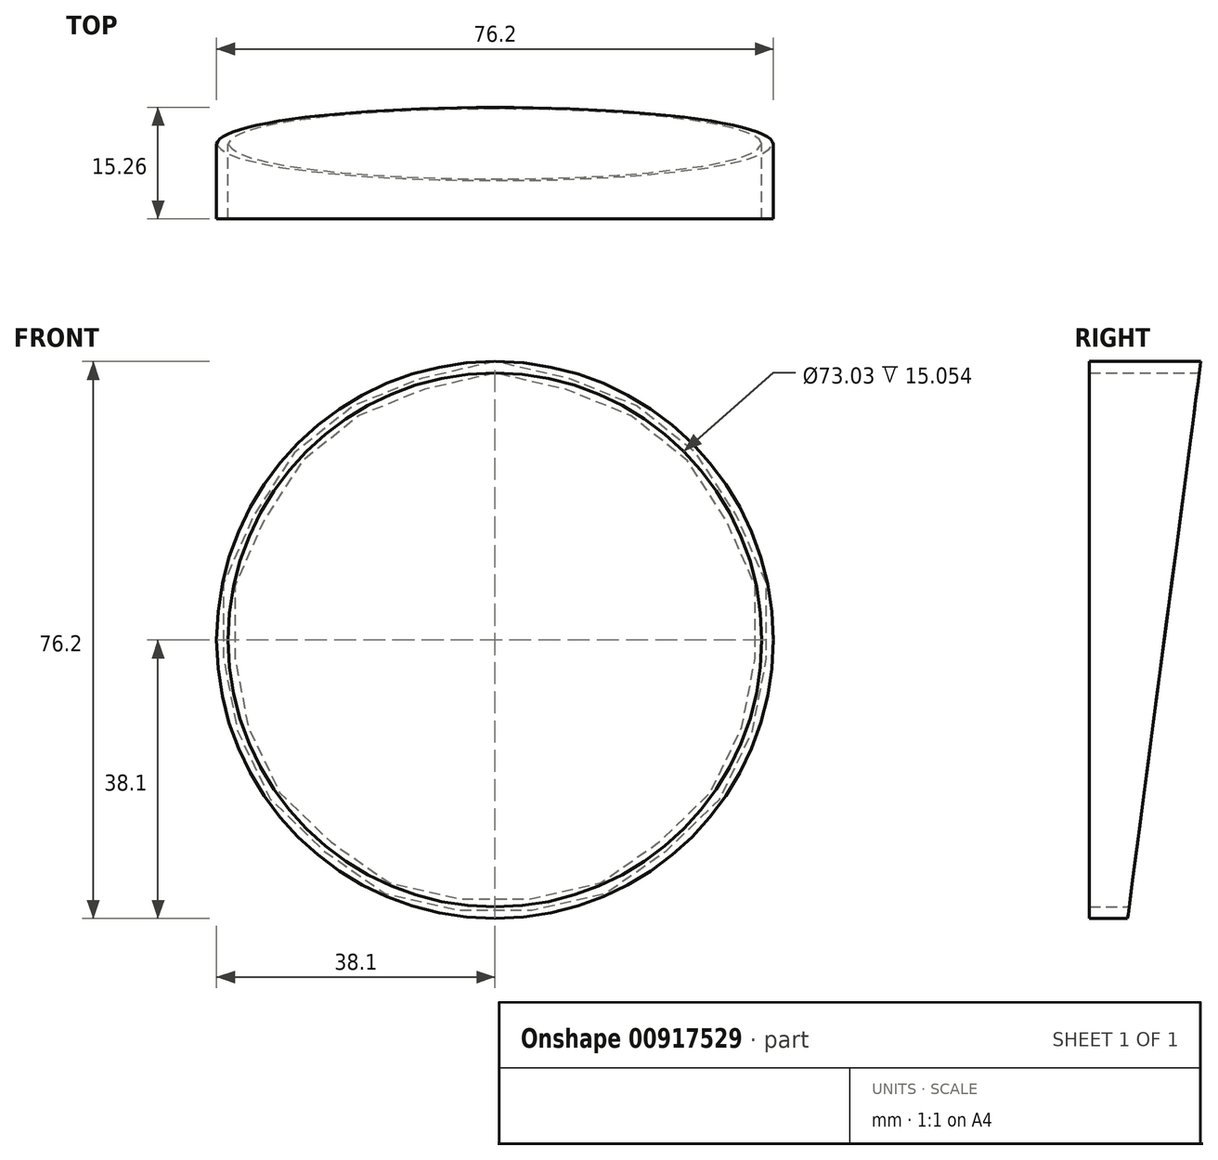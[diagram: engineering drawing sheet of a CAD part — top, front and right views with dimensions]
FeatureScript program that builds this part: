
annotation { "Feature Type Name" : "Feature", "Feature Type Description" : "" }
export const myFeature = defineFeature(function(context is Context, id is Id, definition is map)
    precondition{}
    {
        {
            var Q0;
            Q0=qCreatedBy(makeId("Front.planeOp"),FACE);
            var sketch = newSketch(context, id + "F0", { "sketchPlane" : qUnion([Q0])});
            skCircle(sketch, "E0", {"center": v(0, 38.1) * mm, "radius": 38.1 * mm});
            skCircle(sketch, "E1", {"center": v(0, 38.1) * mm, "radius": 36.51 * mm});
            skPoint(sketch, "E2", {"position": v(0, 0) * mm});
            skSolve(sketch);
        }
        {
            var Q0;
            Q0 = qSketchRegion(id + "F0", true);
            extrude(context, id + "F1", {"entities" : qUnion([Q0]), "endBound" : BoundingType.SYMMETRIC, "depth" : 19.9 * mm, "offsetDistance" : 25.4 * mm});
        }
        {
            var Q0;
            Q0=qCreatedBy(makeId("Right.planeOp"),FACE);
            var sketch = newSketch(context, id + "F2", { "sketchPlane" : qUnion([Q0])});
            skLineSegment(sketch, "E3", {"start": v(5.32, 76.2) * mm, "end": v(-5.94, -9.31) * mm});
            skLineSegment(sketch, "E4", {"start": v(-5.94, -9.31) * mm, "end": v(10.79, -9.31) * mm});
            skLineSegment(sketch, "E5", {"start": v(10.79, -9.31) * mm, "end": v(10.79, 76.2) * mm});
            skLineSegment(sketch, "E6", {"start": v(10.79, 76.2) * mm, "end": v(5.32, 76.2) * mm});
            skSolve(sketch);
        }
        {
            var Q0;
            Q0 = qSketchRegion(id + "F2", true);
            extrude(context, id + "F3", {"entities" : qUnion([Q0]), "operationType" : NewBodyOperationType.REMOVE, "endBound" : BoundingType.SYMMETRIC, "oppositeDirection" : true, "depth" : 76.2 * mm, "offsetDistance" : 25.4 * mm});
        }
    });
